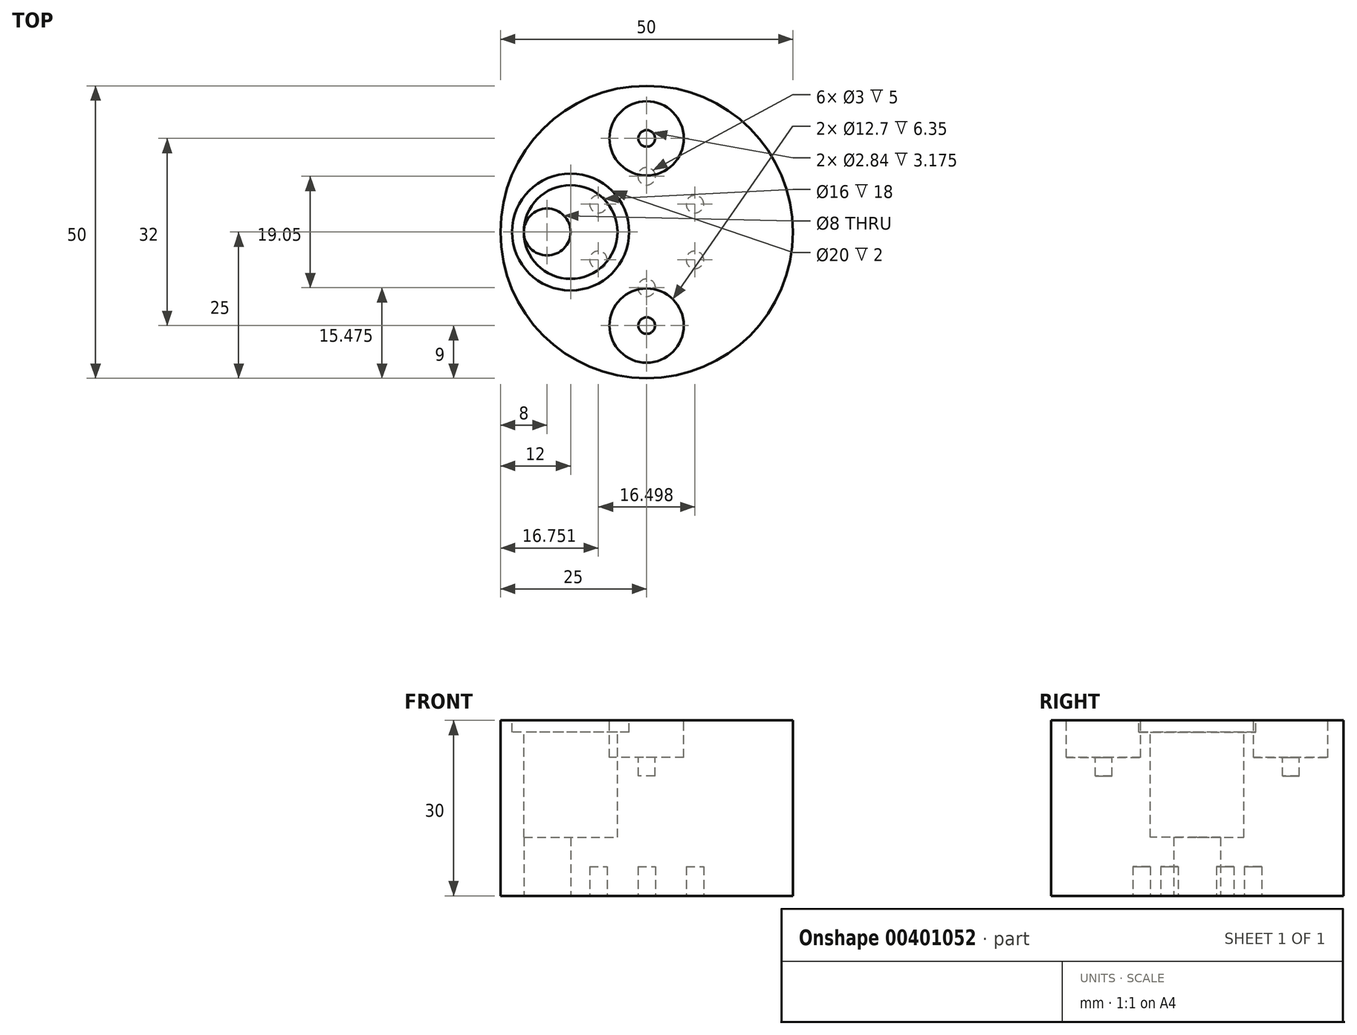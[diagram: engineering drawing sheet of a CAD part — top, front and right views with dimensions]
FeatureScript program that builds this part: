
annotation { "Feature Type Name" : "Feature", "Feature Type Description" : "" }
export const myFeature = defineFeature(function(context is Context, id is Id, definition is map)
    precondition{}
    {
        {
            var Q0;
            Q0=qCreatedBy(makeId("Top.planeOp"),FACE);
            var sketch = newSketch(context, id + "F0", { "sketchPlane" : qUnion([Q0])});
            skCircle(sketch, "E0", {"center": v(0, 0) * mm, "radius": 25 * mm});
            skSolve(sketch);
        }
        {
            var Q0;
            Q0=makeQuery(id+"F0.imprint","IMPRINT",FACE,{"disambiguationData":[TD([[makeQuery(id+"F0.imprint","IMPRINT",EDGE,{"derivedFrom":sQuery(id+"F0.wireOp",EDGE,"E0")}),1.0]])]});
            extrude(context, id + "F1", {"entities" : qUnion([Q0]), "depth" : 30 * mm});
        }
        {
            var Q0;
            Q0=makeQuery(id+"F1.opExtrude","CAP_FACE",FACE,{"disambiguationData":[OSD([sQuery(id+"F0.wireOp",EDGE,"E0")])],"isStart":true});
            var sketch = newSketch(context, id + "F2", { "sketchPlane" : qUnion([Q0])});
            skCircle(sketch, "E1", {"center": v(0, 9.53) * mm, "radius": 1.5 * mm});
            skCircle(sketch, "E2.1.0", {"center": v(-8.25, 4.76) * mm, "radius": 1.5 * mm});
            skCircle(sketch, "E2.2.0", {"center": v(-8.25, -4.76) * mm, "radius": 1.5 * mm});
            skCircle(sketch, "E2.3.0", {"center": v(0, -9.53) * mm, "radius": 1.5 * mm});
            skCircle(sketch, "E2.4.0", {"center": v(8.25, -4.76) * mm, "radius": 1.5 * mm});
            skCircle(sketch, "E2.5.0", {"center": v(8.25, 4.76) * mm, "radius": 1.5 * mm});
            skPoint(sketch, "E2.center", {"position": v(0, 0) * mm});
            skSolve(sketch);
        }
        {
            var Q0;
            Q0=makeQuery(id+"F2.imprint","IMPRINT",FACE,{"disambiguationData":[TD([[makeQuery(id+"F2.imprint","IMPRINT",EDGE,{"derivedFrom":sQuery(id+"F2.wireOp",EDGE,"E1")}),1.0]])]});
            var Q1;
            Q1=makeQuery(id+"F2.imprint","IMPRINT",FACE,{"disambiguationData":[TD([[makeQuery(id+"F2.imprint","IMPRINT",EDGE,{"derivedFrom":sQuery(id+"F2.wireOp",EDGE,"E2.1.0")}),1.0]])]});
            var Q2;
            Q2=makeQuery(id+"F2.imprint","IMPRINT",FACE,{"disambiguationData":[TD([[makeQuery(id+"F2.imprint","IMPRINT",EDGE,{"derivedFrom":sQuery(id+"F2.wireOp",EDGE,"E2.2.0")}),1.0]])]});
            var Q3;
            Q3=makeQuery(id+"F2.imprint","IMPRINT",FACE,{"disambiguationData":[TD([[makeQuery(id+"F2.imprint","IMPRINT",EDGE,{"derivedFrom":sQuery(id+"F2.wireOp",EDGE,"E2.3.0")}),1.0]])]});
            var Q4;
            Q4=makeQuery(id+"F2.imprint","IMPRINT",FACE,{"disambiguationData":[TD([[makeQuery(id+"F2.imprint","IMPRINT",EDGE,{"derivedFrom":sQuery(id+"F2.wireOp",EDGE,"E2.4.0")}),1.0]])]});
            var Q5;
            Q5=makeQuery(id+"F2.imprint","IMPRINT",FACE,{"disambiguationData":[TD([[makeQuery(id+"F2.imprint","IMPRINT",EDGE,{"derivedFrom":sQuery(id+"F2.wireOp",EDGE,"E2.5.0")}),1.0]])]});
            extrude(context, id + "F3", {"entities" : qUnion([Q0, Q1, Q2, Q3, Q4, Q5]), "operationType" : NewBodyOperationType.REMOVE, "oppositeDirection" : true, "depth" : 5 * mm});
        }
        {
            var Q0;
            Q0=makeQuery(id+"F1.opExtrude","CAP_FACE",FACE,{"disambiguationData":[OSD([sQuery(id+"F0.wireOp",EDGE,"E0")])],"isStart":false});
            var sketch = newSketch(context, id + "F4", { "sketchPlane" : qUnion([Q0])});
            skCircle(sketch, "E3", {"center": v(0, 16) * mm, "radius": 6.35 * mm});
            skCircle(sketch, "E4", {"center": v(0, 16) * mm, "radius": 1.42 * mm});
            skCircle(sketch, "E5.1.0", {"center": v(0, -16) * mm, "radius": 6.35 * mm});
            skCircle(sketch, "E5.1.1", {"center": v(0, -16) * mm, "radius": 1.42 * mm});
            skPoint(sketch, "E5.center", {"position": v(0, 0) * mm});
            skCircle(sketch, "E6", {"center": v(-13, 0) * mm, "radius": 8 * mm});
            skCircle(sketch, "E7.0", {"center": v(-13, 0) * mm, "radius": 10 * mm});
            skSolve(sketch);
        }
        {
            var Q0;
            Q0=makeQuery(id+"F4.imprint","IMPRINT",FACE,{"disambiguationData":[TD([[makeQuery(id+"F4.imprint","IMPRINT",EDGE,{"derivedFrom":sQuery(id+"F4.wireOp",EDGE,"E3")}),1.0]])]});
            extrude(context, id + "F5", {"entities" : qUnion([Q0]), "operationType" : NewBodyOperationType.REMOVE, "oppositeDirection" : true, "depth" : 6.35 * mm});
        }
        {
            var Q0;
            Q0=makeQuery(id+"F5.boolean.opBoolean","SPLIT",FACE,{"disambiguationData":[TD([makeQuery(id+"F5.opExtrude","SWEPT_FACE",FACE,{"disambiguationData":[OSD([sQuery(id+"F4.wireOp",EDGE,"E4")])]})])],"derivedFrom":makeQuery(id+"F1.opExtrude","CAP_FACE",FACE,{"disambiguationData":[OSD([sQuery(id+"F0.wireOp",EDGE,"E0")])],"isStart":false})});
            extrude(context, id + "F6", {"entities" : qUnion([Q0]), "operationType" : NewBodyOperationType.REMOVE, "oppositeDirection" : true, "depth" : 9.52 * mm});
        }
        {
            var Q0;
            Q0=makeQuery(id+"F4.imprint","IMPRINT",FACE,{"disambiguationData":[TD([[makeQuery(id+"F4.imprint","IMPRINT",EDGE,{"derivedFrom":sQuery(id+"F4.wireOp",EDGE,"E5.1.0")}),1.0]])]});
            extrude(context, id + "F7", {"entities" : qUnion([Q0]), "operationType" : NewBodyOperationType.REMOVE, "oppositeDirection" : true, "depth" : 6.35 * mm});
        }
        {
            var Q0;
            Q0=makeQuery(id+"F4.imprint","IMPRINT",FACE,{"disambiguationData":[TD([[makeQuery(id+"F4.imprint","IMPRINT",EDGE,{"derivedFrom":sQuery(id+"F4.wireOp",EDGE,"E5.1.1")}),1.0]])]});
            extrude(context, id + "F8", {"entities" : qUnion([Q0]), "operationType" : NewBodyOperationType.REMOVE, "oppositeDirection" : true, "depth" : 9.52 * mm});
        }
        {
            var Q0;
            Q0=makeQuery(id+"F4.imprint","IMPRINT",FACE,{"disambiguationData":[TD([[makeQuery(id+"F4.imprint","IMPRINT",EDGE,{"derivedFrom":sQuery(id+"F4.wireOp",EDGE,"E6")}),1.0]])]});
            extrude(context, id + "F9", {"entities" : qUnion([Q0]), "operationType" : NewBodyOperationType.REMOVE, "oppositeDirection" : true, "depth" : 20 * mm});
        }
        {
            var Q0;
            Q0=makeQuery(id+"F1.opExtrude","CAP_FACE",FACE,{"disambiguationData":[OSD([sQuery(id+"F0.wireOp",EDGE,"E0")])],"isStart":true});
            var sketch = newSketch(context, id + "F10", { "sketchPlane" : qUnion([Q0])});
            skCircle(sketch, "E8", {"center": v(-17, 0) * mm, "radius": 4 * mm});
            skSolve(sketch);
        }
        {
            var Q0;
            Q0=makeQuery(id+"F10.imprint","IMPRINT",FACE,{"disambiguationData":[TD([[makeQuery(id+"F10.imprint","IMPRINT",EDGE,{"derivedFrom":sQuery(id+"F10.wireOp",EDGE,"E8")}),1.0]])]});
            extrude(context, id + "F11", {"entities" : qUnion([Q0]), "operationType" : NewBodyOperationType.REMOVE, "endBound" : BoundingType.THROUGH_ALL, "oppositeDirection" : true, "depth" : 25 * mm});
        }
        {
            var Q0;
            Q0=makeQuery(id+"F4.imprint","IMPRINT",FACE,{"disambiguationData":[TD([[makeQuery(id+"F4.imprint","IMPRINT",EDGE,{"derivedFrom":sQuery(id+"F4.wireOp",EDGE,"E6")}),-1.0]])]});
            extrude(context, id + "F12", {"entities" : qUnion([Q0]), "operationType" : NewBodyOperationType.REMOVE, "oppositeDirection" : true, "depth" : 2 * mm});
        }
    });
